# Revit family: SW1-FaceBased
name_source: partatom
category: Lighting Fixtures
revit_build: Autodesk Revit 2014 (Build: 20130308_1515(x64)
units: mm (PartAtom-declared; Revit-internal decimal feet)

## types (1)
- SW1
    Body = Powder Coat-Kim-Black
    Color Filter = 16777215
    Default Elevation = 48 "
    Description = Site Wallforms are constructed of heavy-duty cast aluminum with a flat tempered glass lens and concealed hardware for vandal resistance. DarkSky compliant with flat glass lens meets IES/IDA full cutoff designation.
    Dimming Lamp Color Temperature Shift = <None>
    Emit Shape Visible in Rendering = No
    Emit from Rectangle Length = 12 "
    Emit from Rectangle Width = 6 "
    Features = Round and triangular geometric shapes
Full-cutoff performance
580nm, 3000K, 4000K and 5000K CCT
    Glass = Glass - Hubbell - White
    IP Rating = IP66
    Lamp = LED
    Manufacturer = KIM Lighting A unit of Hubbell Lighting
    Model = Site Wallforms
    Photometric Note = For more photometric file please find the above link
    Photometric Web File = sw1-18l3k.ies
    Photometric Web Link = https://www.hubbell.com
    Product Doucumentation Link = https://hubbellcdn.com
    Product Page URL = https://www.hubbell.com
    Tilt Angle = -90.00°
    Type Comments = Light Fixture
    URL = https://www.hubbell.com
    Wattage Comments = 15

## geometry (parser evidence)
native form markers: Sweep x1
no freeform markers — native parametric forms only
